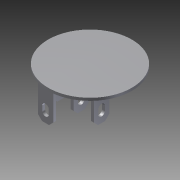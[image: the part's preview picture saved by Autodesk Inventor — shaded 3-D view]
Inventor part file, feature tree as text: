
AUTODESK INVENTOR PART (.ipt)
format: ipt  version: 2014 (Build 180170000, 170)  size: 161,280 bytes
history: native  units: in
note: dims shown in document units (in); Inventor stores cm internally (conversion verified against a paired STEP export)
features: other x7, extrude x6, sketch x6
ambient origin geometry x8: Origin, YZ Plane, XZ Plane, XY Plane, X Axis, Y Axis, Z Axis, Center Point
bodies: Solid1 (feature_tree)
feature tree (19):
  extrude  "Extrusion1"  Depth=0.02in TaperAngle=0.0deg
  extrude  "Extrusion2"  Depth=0.02in TaperAngle=0.0deg
  extrude  "Extrusion3"  Depth=0.02in TaperAngle=0.0deg
  extrude  "Extrusion4"  [1 undecoded]
  extrude  "Extrusion5"  [1 undecoded]
  extrude  "Extrusion6"  [1 undecoded]
  other  "terminal_to_body_XY"
  other  "terminal_to_body_YZ"
  other  "terminal_to_body_ZX"
  other  "terminal_to_body_X"
  other  "terminal_to_body_Y"
  other  "terminal_to_body_Z"
  other  "terminal_to_body_Center"
  sketch  "Sketch_1"  dims[d0=0.0192in d1=0.0in d2=0.02in d3=0.0in]
  sketch  "Sketch_8"
  sketch  "Sketch_7"  dims[d8=0.02in d9=0.0in d10=0.02in d11=0.0in]
  sketch  "Sketch_9"
  sketch  "Sketch_2"  dims[d4=0.02in d5=0.0in d6=0.02in d7=0.0in]
  sketch  "Sketch_11"
note: 3 required parameter values undecoded (feature->parameter linkage not recoverable at this tier; creation-order binding heuristic only, values carry confidence <= 0.55)
